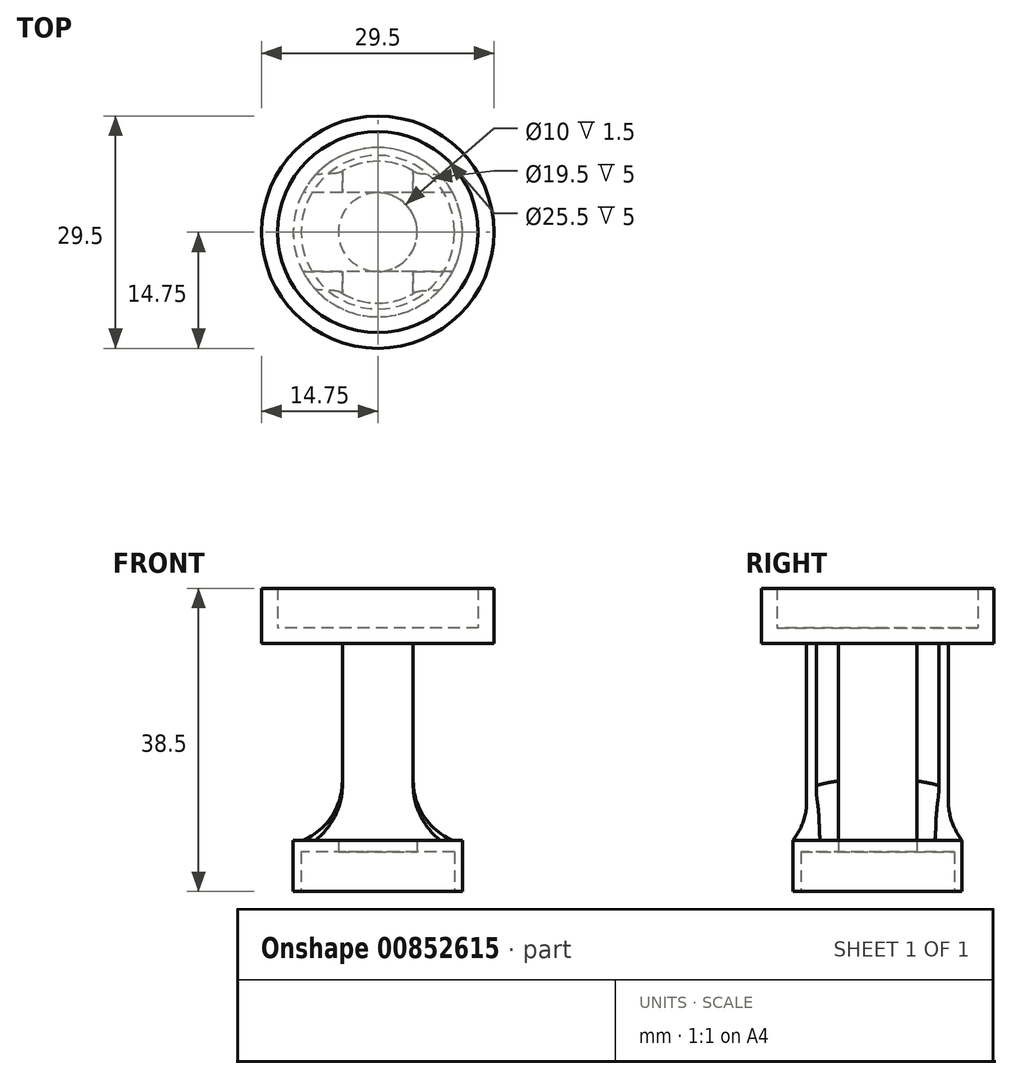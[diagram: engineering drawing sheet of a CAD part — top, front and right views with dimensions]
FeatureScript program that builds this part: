
annotation { "Feature Type Name" : "Feature", "Feature Type Description" : "" }
export const myFeature = defineFeature(function(context is Context, id is Id, definition is map)
    precondition{}
    {
        {
            var Q0;
            Q0=qCreatedBy(makeId("Top.planeOp"),FACE);
            var sketch = newSketch(context, id + "F0", { "sketchPlane" : qUnion([Q0])});
            skCircle(sketch, "E0", {"center": v(0, 0) * mm, "radius": 10.75 * mm});
            skCircle(sketch, "E1", {"center": v(0, 0) * mm, "radius": 9.75 * mm});
            skSolve(sketch);
        }
        {
            var Q0;
            Q0=makeQuery(id+"F0.imprint","IMPRINT",FACE,{"disambiguationData":[TD([[makeQuery(id+"F0.imprint","IMPRINT",EDGE,{"derivedFrom":sQuery(id+"F0.wireOp",EDGE,"E0")}),1.0]])]});
            extrude(context, id + "F1", {"entities" : qUnion([Q0]), "depth" : 5 * mm, "offsetDistance" : 25 * mm});
        }
        {
            var Q0;
            Q0=makeQuery(id+"F1.opExtrude","CAP_FACE",FACE,{"disambiguationData":[OSD([sQuery(id+"F0.wireOp",EDGE,"E0"),sQuery(id+"F0.wireOp",EDGE,"E1")])],"isStart":false});
            var sketch = newSketch(context, id + "F2", { "sketchPlane" : qUnion([Q0])});
            skCircle(sketch, "E2", {"center": v(0, 0) * mm, "radius": 9.75 * mm});
            skCircle(sketch, "E3", {"center": v(0, 0) * mm, "radius": 5 * mm});
            skCircle(sketch, "E4", {"center": v(0, 0) * mm, "radius": 9 * mm});
            skSolve(sketch);
        }
        {
            var Q0;
            Q0=makeQuery(id+"F2.imprint","IMPRINT",FACE,{"disambiguationData":[TD([[makeQuery(id+"F2.imprint","IMPRINT",EDGE,{"derivedFrom":sQuery(id+"F2.wireOp",EDGE,"E2")}),1.0]])]});
            var Q1;
            Q1=makeQuery(id+"F2.imprint","IMPRINT",FACE,{"disambiguationData":[TD([[makeQuery(id+"F2.imprint","IMPRINT",EDGE,{"derivedFrom":sQuery(id+"F2.wireOp",EDGE,"E2")}),-1.0]])]});
            var Q2;
            Q2=makeQuery(id+"F2.imprint","IMPRINT",FACE,{"disambiguationData":[TD([[makeQuery(id+"F2.imprint","IMPRINT",EDGE,{"derivedFrom":sQuery(id+"F2.wireOp",EDGE,"E3")}),-1.0]])]});
            extrude(context, id + "F3", {"entities" : qUnion([Q0, Q1, Q2]), "operationType" : NewBodyOperationType.ADD, "depth" : 1.5 * mm, "offsetDistance" : 25 * mm});
        }
        {
            var Q0;
            Q0=makeQuery(id+"F2.imprint","IMPRINT",FACE,{"disambiguationData":[TD([[makeQuery(id+"F2.imprint","IMPRINT",EDGE,{"derivedFrom":sQuery(id+"F2.wireOp",EDGE,"E3")}),-1.0]])]});
            extrude(context, id + "F4", {"entities" : qUnion([Q0]), "operationType" : NewBodyOperationType.ADD, "depth" : 26.5 * mm, "offsetDistance" : 25 * mm});
        }
        {
            var Q0;
            Q0=qCreatedBy(makeId("Front.planeOp"),FACE);
            var sketch = newSketch(context, id + "F5", { "sketchPlane" : qUnion([Q0])});
            skLineSegment(sketch, "E5.bottom", {"start": v(4.5, 36.5) * mm, "end": v(-4.5, 36.5) * mm});
            skLineSegment(sketch, "E5.top", {"start": v(4.5, 6.5) * mm, "end": v(-4.5, 6.5) * mm});
            skLineSegment(sketch, "E5.left", {"start": v(4.5, 36.5) * mm, "end": v(4.5, 6.5) * mm});
            skLineSegment(sketch, "E5.right", {"start": v(-4.5, 36.5) * mm, "end": v(-4.5, 6.5) * mm});
            skPoint(sketch, "E5.middle", {"position": v(0, 21.5) * mm});
            skLineSegment(sketch, "E6", {"start": v(4.5, 31.5) * mm, "end": v(9.61, 31.5) * mm});
            skLineSegment(sketch, "E7", {"start": v(9.61, 31.5) * mm, "end": v(9.61, 6.5) * mm});
            skLineSegment(sketch, "E8", {"start": v(9.61, 6.5) * mm, "end": v(4.5, 6.5) * mm});
            skLineSegment(sketch, "E9.MirrorCS", {"start": v(-4.5, 31.5) * mm, "end": v(-9.61, 31.5) * mm});
            skLineSegment(sketch, "E10.MirrorCS", {"start": v(-9.61, 31.5) * mm, "end": v(-9.61, 6.5) * mm});
            skLineSegment(sketch, "E11.MirrorCS", {"start": v(-9.61, 6.5) * mm, "end": v(-4.5, 6.5) * mm});
            skSolve(sketch);
        }
        {
            var Q0;
            {var subQ2=sQuery(id+"F5.wireOp",EDGE,"E9.MirrorCS");Q0=makeQuery(id+"F5.imprint","IMPRINT",FACE,{"disambiguationData":[TD([[makeQuery(id+"F5.imprint","IMPRINT",EDGE,{"derivedFrom":subQ2}),1.0]])]});}
            var Q1;
            {var subQ2=sQuery(id+"F5.wireOp",EDGE,"E6");Q1=makeQuery(id+"F5.imprint","IMPRINT",FACE,{"disambiguationData":[TD([[makeQuery(id+"F5.imprint","IMPRINT",EDGE,{"derivedFrom":subQ2}),-1.0]])]});}
            extrude(context, id + "F6", {"entities" : qUnion([Q0, Q1]), "operationType" : NewBodyOperationType.REMOVE, "oppositeDirection" : true, "depth" : 25 * mm, "offsetDistance" : 25 * mm, "symmetric" : true});
        }
        {
            var Q0;
            Q0=qCreatedBy(makeId("Right.planeOp"),FACE);
            var sketch = newSketch(context, id + "F7", { "sketchPlane" : qUnion([Q0])});
            skLineSegment(sketch, "E12.bottom", {"start": v(-5, 39.8) * mm, "end": v(5, 39.8) * mm});
            skLineSegment(sketch, "E12.top", {"start": v(-5, 6.5) * mm, "end": v(5, 6.5) * mm});
            skLineSegment(sketch, "E12.left", {"start": v(-5, 39.8) * mm, "end": v(-5, 6.5) * mm});
            skLineSegment(sketch, "E12.right", {"start": v(5, 39.8) * mm, "end": v(5, 6.5) * mm});
            skPoint(sketch, "E12.middle", {"position": v(0, 23.15) * mm});
            skSolve(sketch);
        }
        {
            var Q0;
            Q0=makeQuery(id+"F7.imprint","IMPRINT",FACE,{"disambiguationData":[TD([[makeQuery(id+"F7.imprint","IMPRINT",EDGE,{"derivedFrom":sQuery(id+"F7.wireOp",EDGE,"E12.bottom")}),-1.0]])]});
            extrude(context, id + "F8", {"entities" : qUnion([Q0]), "operationType" : NewBodyOperationType.REMOVE, "depth" : 25 * mm, "offsetDistance" : 25 * mm, "symmetric" : true});
        }
        {
            var Q0;
            Q0=makeQuery(id+"F6.boolean.opBoolean","SPLIT",FACE,{"disambiguationData":[OD(0.0)],"derivedFrom":makeQuery(id+"F4.opExtrude","CAP_FACE",FACE,{"disambiguationData":[OSD([sQuery(id+"F2.wireOp",EDGE,"E3"),sQuery(id+"F2.wireOp",EDGE,"E4")])],"isStart":false})});
            var sketch = newSketch(context, id + "F9", { "sketchPlane" : qUnion([Q0])});
            skCircle(sketch, "E13", {"center": v(0, 0) * mm, "radius": 12.75 * mm});
            skCircle(sketch, "E14", {"center": v(0, 0) * mm, "radius": 14.75 * mm});
            skSolve(sketch);
        }
        {
            var Q0;
            Q0=makeQuery(id+"F9.imprint","IMPRINT",FACE,{"disambiguationData":[TD([[makeQuery(id+"F9.imprint","IMPRINT",EDGE,{"derivedFrom":sQuery(id+"F9.wireOp",EDGE,"E13")}),1.0]])]});
            var Q1;
            {var subQ0=sQuery(id+"F2.wireOp",EDGE,"E4");Q1=makeQuery(id+"F9.imprint","IMPRINT",FACE,{"disambiguationData":[TD([[makeQuery(id+"F9.imprint","IMPRINT",EDGE,{"derivedFrom":makeQuery(id+"F6.boolean.opBoolean","SPLIT",EDGE,{"disambiguationData":[OD(0.0)],"derivedFrom":makeQuery(id+"F4.opExtrude","CAP_EDGE",EDGE,{"disambiguationData":[OSD([subQ0])],"isStart":false})})}),1.0]])]});}
            extrude(context, id + "F10", {"entities" : qUnion([Q0, Q1]), "operationType" : NewBodyOperationType.ADD, "depth" : 2 * mm, "offsetDistance" : 25 * mm});
        }
        {
            var Q0;
            Q0=makeQuery(id+"F9.imprint","IMPRINT",FACE,{"disambiguationData":[TD([[makeQuery(id+"F9.imprint","IMPRINT",EDGE,{"derivedFrom":sQuery(id+"F9.wireOp",EDGE,"E13")}),-1.0]])]});
            extrude(context, id + "F11", {"entities" : qUnion([Q0]), "operationType" : NewBodyOperationType.ADD, "depth" : 7 * mm, "offsetDistance" : 25 * mm});
        }
        {
            var Q0;
            Q0=makeQuery(id+"F6.boolean.opBoolean","SPLIT",EDGE,{"disambiguationData":[OD(0.0)],"derivedFrom":makeQuery(id+"F4.boolean.opBoolean","INTERSECT",EDGE,{"derivedFrom":[makeQuery(id+"F3.opExtrude","CAP_FACE",FACE,{"disambiguationData":[OSD([sQuery(id+"F0.wireOp",EDGE,"E0"),sQuery(id+"F2.wireOp",EDGE,"E3")])],"isStart":false}),makeQuery(id+"F4.opExtrude","SWEPT_FACE",FACE,{"disambiguationData":[OSD([sQuery(id+"F2.wireOp",EDGE,"E4")])]})]})});
            var Q1;
            Q1=makeQuery(id+"F6.boolean.opBoolean","COPY",EDGE,{"disambiguationData":[OD(0.0)],"derivedFrom":makeQuery(id+"F6.opExtrude","SWEPT_EDGE",EDGE,{"disambiguationData":[OSD([sQuery(id+"F5.wireOp",EDGE,"E5.top"),sQuery(id+"F5.wireOp",EDGE,"E5.right"),sQuery(id+"F5.wireOp",EDGE,"E11.MirrorCS")])]})});
            var Q2;
            Q2=makeQuery(id+"F6.boolean.opBoolean","COPY",EDGE,{"disambiguationData":[OD(0.0)],"derivedFrom":makeQuery(id+"F6.opExtrude","SWEPT_EDGE",EDGE,{"disambiguationData":[OSD([sQuery(id+"F5.wireOp",EDGE,"E5.top"),sQuery(id+"F5.wireOp",EDGE,"E5.left"),sQuery(id+"F5.wireOp",EDGE,"E8")])]})});
            var Q3;
            Q3=makeQuery(id+"F6.boolean.opBoolean","COPY",EDGE,{"disambiguationData":[OD(1.0)],"derivedFrom":makeQuery(id+"F6.opExtrude","SWEPT_EDGE",EDGE,{"disambiguationData":[OSD([sQuery(id+"F5.wireOp",EDGE,"E5.top"),sQuery(id+"F5.wireOp",EDGE,"E5.left"),sQuery(id+"F5.wireOp",EDGE,"E8")])]})});
            var Q4;
            Q4=makeQuery(id+"F6.boolean.opBoolean","SPLIT",EDGE,{"disambiguationData":[OD(1.0)],"derivedFrom":makeQuery(id+"F4.boolean.opBoolean","INTERSECT",EDGE,{"derivedFrom":[makeQuery(id+"F3.opExtrude","CAP_FACE",FACE,{"disambiguationData":[OSD([sQuery(id+"F0.wireOp",EDGE,"E0"),sQuery(id+"F2.wireOp",EDGE,"E3")])],"isStart":false}),makeQuery(id+"F4.opExtrude","SWEPT_FACE",FACE,{"disambiguationData":[OSD([sQuery(id+"F2.wireOp",EDGE,"E4")])]})]})});
            var Q5;
            Q5=makeQuery(id+"F6.boolean.opBoolean","COPY",EDGE,{"disambiguationData":[OD(1.0)],"derivedFrom":makeQuery(id+"F6.opExtrude","SWEPT_EDGE",EDGE,{"disambiguationData":[OSD([sQuery(id+"F5.wireOp",EDGE,"E5.top"),sQuery(id+"F5.wireOp",EDGE,"E5.right"),sQuery(id+"F5.wireOp",EDGE,"E11.MirrorCS")])]})});
            var Q6;
            Q6=makeQuery(id+"F6.boolean.opBoolean","SPLIT",EDGE,{"disambiguationData":[OD(1.0)],"derivedFrom":makeQuery(id+"F4.opExtrude","CAP_EDGE",EDGE,{"disambiguationData":[OSD([sQuery(id+"F2.wireOp",EDGE,"E4")])],"isStart":false})});
            var Q7;
            Q7=makeQuery(id+"F6.boolean.opBoolean","COPY",EDGE,{"disambiguationData":[OD(1.0)],"derivedFrom":makeQuery(id+"F6.opExtrude","SWEPT_EDGE",EDGE,{"disambiguationData":[OSD([sQuery(id+"F5.wireOp",EDGE,"E5.left"),sQuery(id+"F5.wireOp",EDGE,"E6")])]})});
            var Q8;
            Q8=makeQuery(id+"F6.boolean.opBoolean","COPY",EDGE,{"disambiguationData":[OD(1.0)],"derivedFrom":makeQuery(id+"F6.opExtrude","SWEPT_EDGE",EDGE,{"disambiguationData":[OSD([sQuery(id+"F5.wireOp",EDGE,"E5.right"),sQuery(id+"F5.wireOp",EDGE,"E9.MirrorCS")])]})});
            var Q9;
            Q9=makeQuery(id+"F6.boolean.opBoolean","SPLIT",EDGE,{"disambiguationData":[OD(0.0)],"derivedFrom":makeQuery(id+"F4.opExtrude","CAP_EDGE",EDGE,{"disambiguationData":[OSD([sQuery(id+"F2.wireOp",EDGE,"E4")])],"isStart":false})});
            var Q10;
            Q10=makeQuery(id+"F6.boolean.opBoolean","COPY",EDGE,{"disambiguationData":[OD(0.0)],"derivedFrom":makeQuery(id+"F6.opExtrude","SWEPT_EDGE",EDGE,{"disambiguationData":[OSD([sQuery(id+"F5.wireOp",EDGE,"E5.right"),sQuery(id+"F5.wireOp",EDGE,"E9.MirrorCS")])]})});
            var Q11;
            Q11=makeQuery(id+"F6.boolean.opBoolean","COPY",EDGE,{"disambiguationData":[OD(0.0)],"derivedFrom":makeQuery(id+"F6.opExtrude","SWEPT_EDGE",EDGE,{"disambiguationData":[OSD([sQuery(id+"F5.wireOp",EDGE,"E5.left"),sQuery(id+"F5.wireOp",EDGE,"E6")])]})});
            var Q12;
            Q12=makeQuery(id+"F8.boolean.opBoolean","INTERSECT",EDGE,{"derivedFrom":[makeQuery(id+"F6.boolean.opBoolean","SPLIT",FACE,{"disambiguationData":[OD(1.0)],"derivedFrom":makeQuery(id+"F4.opExtrude","CAP_FACE",FACE,{"disambiguationData":[OSD([sQuery(id+"F2.wireOp",EDGE,"E3"),sQuery(id+"F2.wireOp",EDGE,"E4")])],"isStart":false})}),makeQuery(id+"F8.opExtrude","SWEPT_FACE",FACE,{"disambiguationData":[OSD([sQuery(id+"F7.wireOp",EDGE,"E12.right")])]})]});
            var Q13;
            Q13=makeQuery(id+"F8.boolean.opBoolean","INTERSECT",EDGE,{"derivedFrom":[makeQuery(id+"F6.boolean.opBoolean","SPLIT",FACE,{"disambiguationData":[OD(0.0)],"derivedFrom":makeQuery(id+"F4.opExtrude","CAP_FACE",FACE,{"disambiguationData":[OSD([sQuery(id+"F2.wireOp",EDGE,"E3"),sQuery(id+"F2.wireOp",EDGE,"E4")])],"isStart":false})}),makeQuery(id+"F8.opExtrude","SWEPT_FACE",FACE,{"disambiguationData":[OSD([sQuery(id+"F7.wireOp",EDGE,"E12.left")])]})]});
            fillet(context, id + "F12", {"entities" : qUnion([Q0, Q1, Q2, Q3, Q4, Q5, Q6, Q7, Q8, Q9, Q10, Q11, Q12, Q13]), "tangentPropagation" : true, "radius" : 8 * mm, "defaultsChanged" : true, "vertexSettings" : [], "allowEdgeOverflow" : false});
        }
    });
